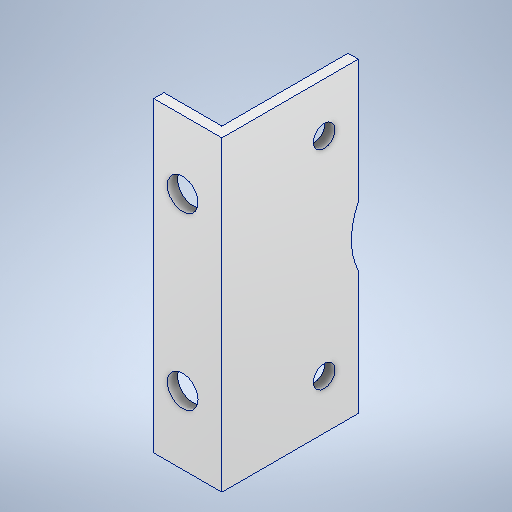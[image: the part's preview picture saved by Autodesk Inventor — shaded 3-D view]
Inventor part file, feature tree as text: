
AUTODESK INVENTOR PART (.ipt)
format: ipt  version: 2025 (Build 290162000, 162)  size: 282,112 bytes
history: native  units: mm
features: sketch x4, extrude x2, hole x2, projected_geometry x2, other x1
ambient origin geometry x8: Origin, YZ Plane, XZ Plane, XY Plane, X Axis, Y Axis, Z Axis, Center Point
bodies: Body1 (feature_tree)
feature tree (11):
  other  "Těleso1"
  extrude  "Vysunutí1"  Depth=20.0mm
  hole  "Díra1"  [1 undecoded]
  hole  "Díra4"  [1 undecoded]
  extrude  "Vysunutí2"  Depth=1.5mm
  sketch  "Náčrt1"
  sketch  "Náčrt2"
  projected_geometry  "Promítnutá smyčka1"
  sketch  "Náčrt5"
  projected_geometry  "Promítnutá smyčka4"
  sketch  "Náčrt6"
note: 2 required parameter values undecoded (feature->parameter linkage not recoverable at this tier; creation-order binding heuristic only, values carry confidence <= 0.55)
